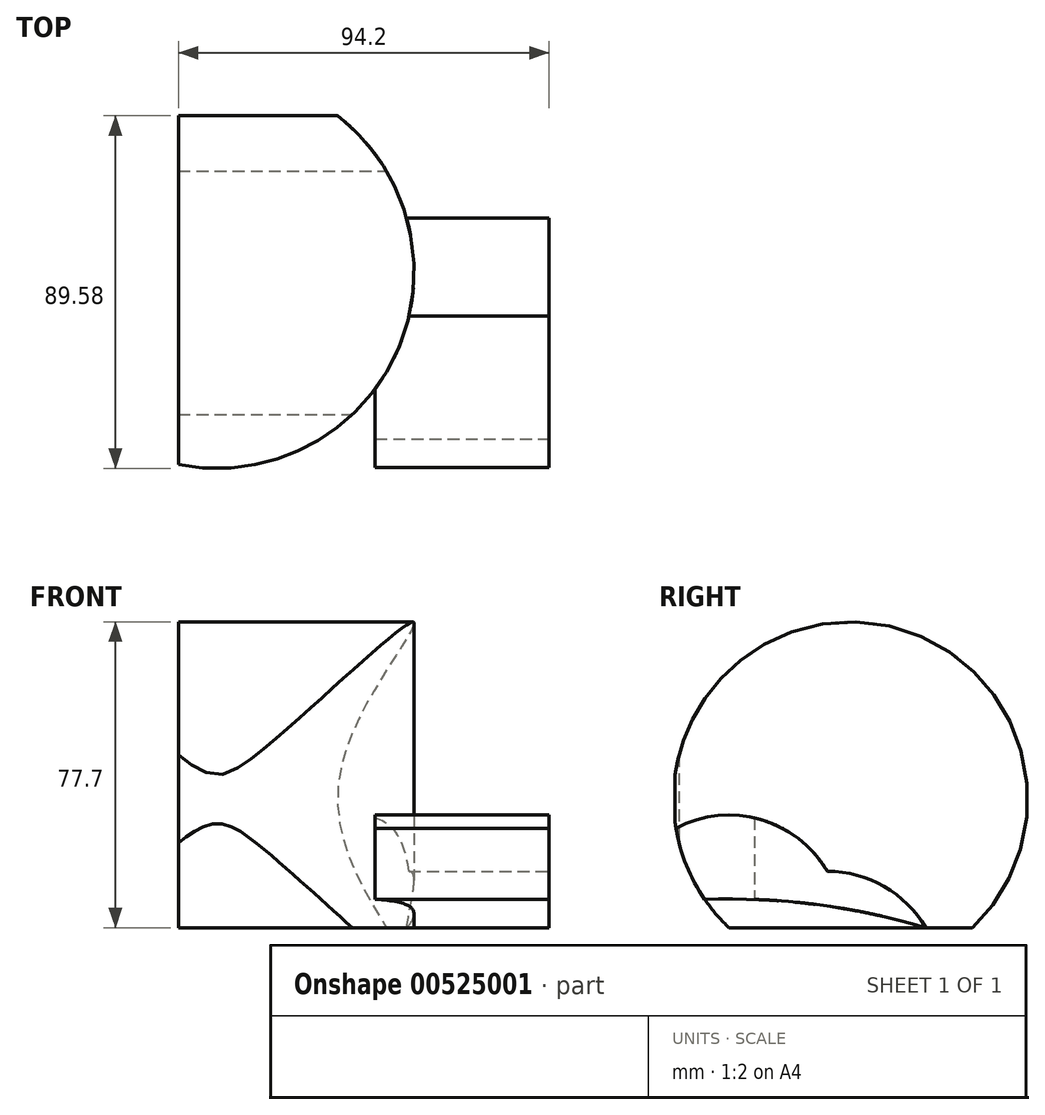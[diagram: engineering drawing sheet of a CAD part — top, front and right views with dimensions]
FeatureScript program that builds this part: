
annotation { "Feature Type Name" : "Feature", "Feature Type Description" : "" }
export const myFeature = defineFeature(function(context is Context, id is Id, definition is map)
    precondition{}
    {
        {
            var Q0;
            Q0=qCreatedBy(makeId("Top.planeOp"),FACE);
            var sketch = newSketch(context, id + "F0", { "sketchPlane" : qUnion([Q0])});
            skLineSegment(sketch, "E0.bottom", {"start": v(-50, -50) * mm, "end": v(50, -50) * mm});
            skLineSegment(sketch, "E0.top", {"start": v(-50, 50) * mm, "end": v(50, 50) * mm});
            skLineSegment(sketch, "E0.left", {"start": v(-50, -50) * mm, "end": v(-50, 50) * mm});
            skLineSegment(sketch, "E0.right", {"start": v(50, -50) * mm, "end": v(50, 50) * mm});
            skSolve(sketch);
        }
        {
            var Q0;
            Q0=qCreatedBy(makeId("Right.planeOp"),FACE);
            cPlane(context, id + "F1", {"entities" : qUnion([Q0]), "cplaneType" : CPlaneType.OFFSET, "offset" : 55.8 * mm, "width" : 150 * mm, "height" : 150 * mm});
        }
        {
            var Q0;
            Q0=makeQuery(id+"F0.imprint","IMPRINT",FACE,{"disambiguationData":[TD([[makeQuery(id+"F0.imprint","IMPRINT",EDGE,{"derivedFrom":sQuery(id+"F0.wireOp",EDGE,"E0.bottom")}),1.0]])]});
            extrude(context, id + "F2", {"entities" : qUnion([Q0]), "depth" : 52 * mm, "offsetDistance" : 25 * mm});
        }
        {
            var Q0;
            Q0=qCreatedBy(id+"F1.planeOp",FACE);
            var sketch = newSketch(context, id + "F3", { "sketchPlane" : qUnion([Q0])});
            skArc(sketch, "E1", {"start": v(-25, 14.3) * mm, "mid": v(-39.4, 10.47) * mm, "end": v(-50, 0) * mm});
            skArc(sketch, "E2", {"start": v(50, 0) * mm, "mid": v(39.4, 10.47) * mm, "end": v(25, 14.3) * mm});
            skArc(sketch, "E3", {"start": v(25, 14.3) * mm, "mid": v(0, 28.6) * mm, "end": v(-25, 14.3) * mm});
            skPoint(sketch, "E4.orphan", {"position": v(0, 0) * mm});
            skArc(sketch, "E5", {"start": v(50, 0) * mm, "mid": v(0, 7.3) * mm, "end": v(-50, 0) * mm});
            skArc(sketch, "E6", {"start": v(-50, 0) * mm, "mid": v(-24.2, -1.87) * mm, "end": v(0, 7.3) * mm});
            skArc(sketch, "E7", {"start": v(-1.02, 6.47) * mm, "mid": v(23.76, -2.5) * mm, "end": v(50, 0) * mm});
            skSolve(sketch);
        }
        {
            var Q0;
            {var subQ4=sQuery(id+"F3.wireOp",EDGE,"E1");Q0=makeQuery(id+"F3.imprint","IMPRINT",FACE,{"disambiguationData":[TD([[makeQuery(id+"F3.imprint","IMPRINT",EDGE,{"derivedFrom":subQ4}),1.0]])]});}
            extrude(context, id + "F4", {"entities" : qUnion([Q0]), "operationType" : NewBodyOperationType.INTERSECT, "oppositeDirection" : true, "depth" : 50 * mm, "offsetDistance" : 25 * mm});
        }
        {
            var Q0;
            Q0=qCreatedBy(makeId("Top.planeOp"),FACE);
            var sketch = newSketch(context, id + "F5", { "sketchPlane" : qUnion([Q0])});
            skCircle(sketch, "E8", {"center": v(-34.34, 36.34) * mm, "radius": 50 * mm});
            skSolve(sketch);
        }
        {
            var Q0;
            Q0=makeQuery(id+"F5.imprint","IMPRINT",FACE,{"disambiguationData":[TD([[makeQuery(id+"F5.imprint","IMPRINT",EDGE,{"derivedFrom":sQuery(id+"F5.wireOp",EDGE,"E8")}),1.0]])]});
            extrude(context, id + "F6", {"entities" : qUnion([Q0]), "operationType" : NewBodyOperationType.ADD, "depth" : 100 * mm, "offsetDistance" : 25 * mm});
        }
        {
            var Q0;
            Q0=qCreatedBy(id+"F1.planeOp",FACE);
            var sketch = newSketch(context, id + "F7", { "sketchPlane" : qUnion([Q0])});
            skCircle(sketch, "E9", {"center": v(30.92, 32.7) * mm, "radius": 45 * mm});
            skSolve(sketch);
        }
        {
            var Q0;
            Q0=makeQuery(id+"F7.imprint","IMPRINT",FACE,{"disambiguationData":[TD([[makeQuery(id+"F7.imprint","IMPRINT",EDGE,{"derivedFrom":sQuery(id+"F7.wireOp",EDGE,"E9")}),1.0]])]});
            extrude(context, id + "F8", {"entities" : qUnion([Q0]), "operationType" : NewBodyOperationType.INTERSECT, "oppositeDirection" : true, "depth" : 100 * mm, "offsetDistance" : 25 * mm});
        }
    });
